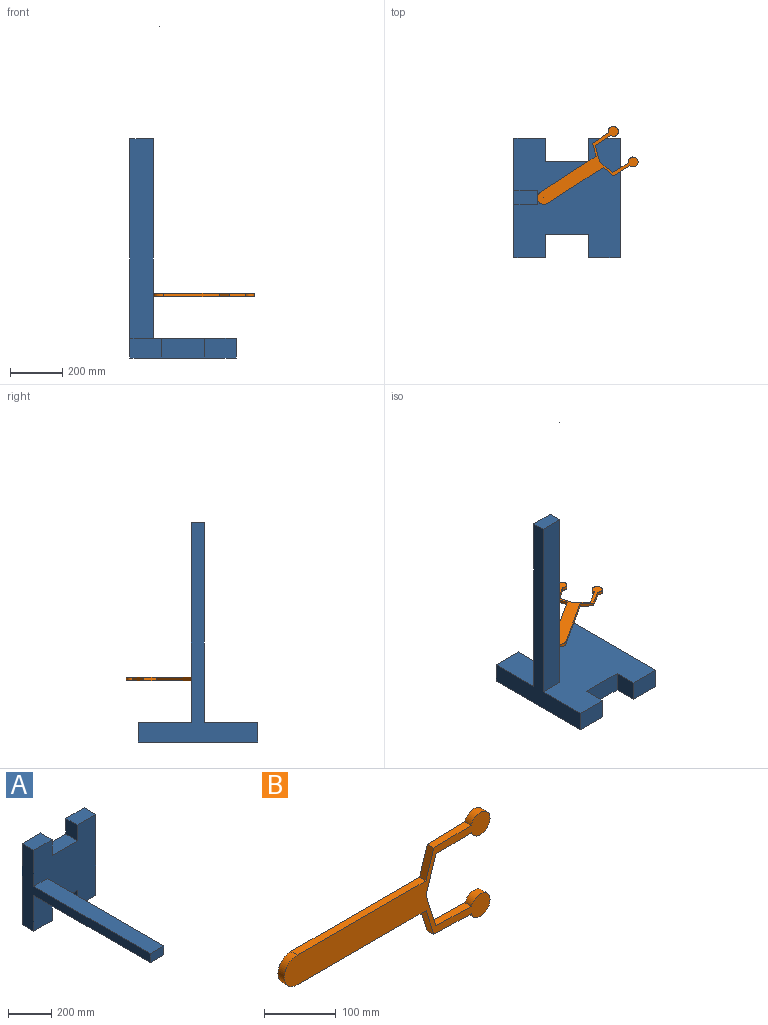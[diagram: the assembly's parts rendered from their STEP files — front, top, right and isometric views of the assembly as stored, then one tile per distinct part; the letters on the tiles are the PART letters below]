
ASSEMBLY  parts=2 mates=2
PART A: 20 faces, bbox 406.4x1270x457.2 mm
  f0: plane 457.2x406.4mm, normal (0,-1,0), area 151935.2mm2, adj f1,f2,f3,f4,f5,f6,f7,f8
  f1: plane 88.9x76.2mm, normal (1,0,0), area 6774.2mm2, adj f0,f2,f12,f13
  f2: plane 120.65x76.2mm, normal (0,0,1), area 9193.5mm2, adj f0,f1,f3,f13
  f3: plane 838.2x457.2mm, normal (-1,0,0), area 73548.2mm2, adj f0,f2,f4,f13,f14,f15,f17
  f4: plane 120.65x76.2mm, normal (0,0,-1), area 9193.5mm2, adj f0,f3,f5,f13
  f5: plane 88.9x76.2mm, normal (1,0,0), area 6774.2mm2, adj f0,f4,f6,f13
  f6: plane 165.1x76.2mm, normal (0,0,-1), area 12580.6mm2, adj f0,f5,f7,f13
  f7: plane 88.9x76.2mm, normal (-1,0,0), area 6774.2mm2, adj f0,f6,f8,f13
  f8: plane 120.65x76.2mm, normal (0,0,-1), area 9193.5mm2, adj f0,f7,f9,f13
  f9: plane 457.2x76.2mm, normal (1,0,0), area 34838.6mm2, adj f0,f8,f10,f13
  f10: plane 120.65x76.2mm, normal (0,0,1), area 9193.5mm2, adj f0,f9,f11,f13
  f11: plane 88.9x76.2mm, normal (-1,0,0), area 6774.2mm2, adj f0,f10,f12,f13
  f12: plane 165.1x76.2mm, normal (0,0,1), area 12580.6mm2, adj f0,f1,f11,f13
  f13: plane 457.2x406.4mm, normal (0,1,0), area 156451.3mm2, adj f1,f2,f3,f4,f5,f6,f7,f8
  f14: plane 762x88.9mm, normal (0,0,1), area 67741.8mm2, adj f0,f3,f16,f17
  f15: plane 762x88.9mm, normal (0,0,-1), area 67741.8mm2, adj f0,f3,f16,f17
  f16: plane 762x50.8mm, normal (1,0,0), area 38709.6mm2, adj f0,f14,f15,f17
  f17: plane 88.9x50.8mm, normal (0,-1,0), area 4516.1mm2, adj f3,f14,f15,f16
  f18: cylinder r=0mm len=1193.8mm, axis (0,1,0), area 9.5mm2, adj f0,f19
  f19: plane 0x0mm, normal (0,-1,0), area 0mm2, adj f18
PART B: 15 faces, bbox 405.6x12.7x177.4 mm
  f0: cylinder r=25.4mm len=50.8mm, axis (0,1,0), area 1013.4mm2, adj f1,f12,f13,f14
  f1: plane 254x12.7mm, normal (0,0,-1), area 3225.8mm2, adj f0,f2,f13,f14
  f2: plane 48.5x15.12mm, normal (-0.95,0,-0.3), area 645.2mm2, adj f1,f3,f13,f14
  f3: plane 73.95x12.7mm, normal (-0.02,0,-1), area 939.4mm2, adj f2,f4,f13,f14
  f4: cylinder r=19.05mm len=38.1mm, axis (0,1,0), area 1355.7mm2, adj f3,f5,f13,f14
  f5: plane 70.25x12.7mm, normal (0.02,0,1), area 892.4mm2, adj f4,f6,f13,f14
  f6: plane 61.29x19.11mm, normal (0.95,0,0.3), area 815.3mm2, adj f5,f7,f13,f14
  f7: plane 61.29x19.11mm, normal (0.95,0,-0.3), area 815.3mm2, adj f6,f8,f13,f14
  f8: plane 70.25x12.7mm, normal (0.02,0,-1), area 892.4mm2, adj f7,f9,f13,f14
  f9: cylinder r=19.05mm len=38.1mm, axis (0,1,0), area 1355.7mm2, adj f8,f10,f13,f14
  f10: plane 73.95x12.7mm, normal (-0.02,0,1), area 939.4mm2, adj f9,f11,f13,f14
  f11: plane 48.5x15.12mm, normal (-0.95,0,0.3), area 645.2mm2, adj f10,f12,f13,f14
  f12: plane 254x12.7mm, normal (0,0,1), area 3225.8mm2, adj f0,f11,f13,f14
  f13: plane 405.62x177.37mm, normal (0,-1,0), area 18879mm2, adj f0,f1,f2,f3,f4,f5,f6,f7
  f14: plane 405.62x177.37mm, normal (0,1,0), area 18879mm2, adj f0,f1,f2,f3,f4,f5,f6,f7
PLACE A rot(axis=(-1,0,0),90deg) t=(-4.72,0,-76.2)mm fixed
PLACE B rot(axis=(-0.92,-0.27,0.27),94.6deg) t=(-93.62,0,158.64)mm
MATE cylindrical B.f0 <-> A.f18  axis (0,0,1) through (-93.62,0,171.34)mm
MATE parallel B.f13 <-> A.f0  axis (0,0,1) through (50.51,92.76,171.34)mm
